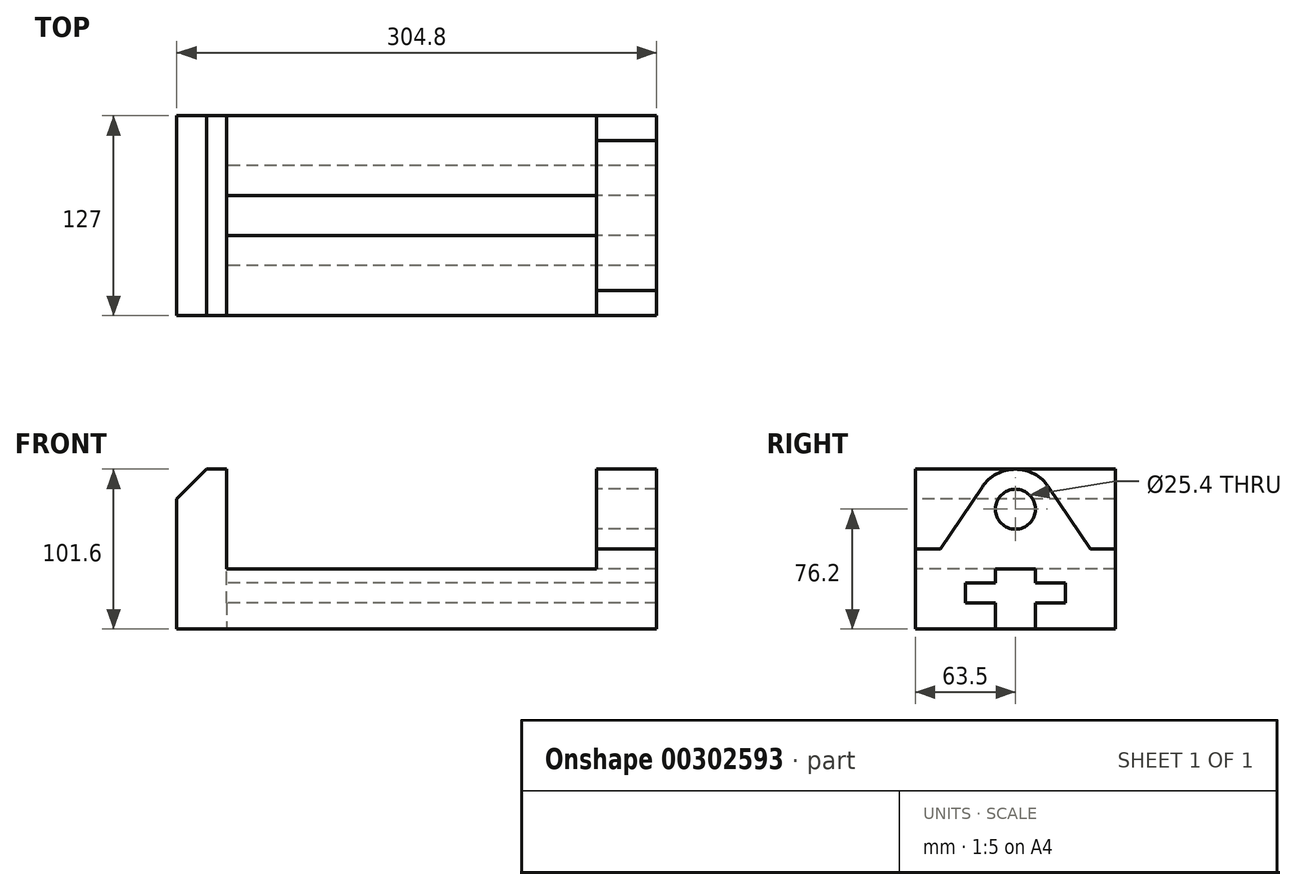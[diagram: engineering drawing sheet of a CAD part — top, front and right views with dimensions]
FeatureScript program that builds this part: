
annotation { "Feature Type Name" : "Feature", "Feature Type Description" : "" }
export const myFeature = defineFeature(function(context is Context, id is Id, definition is map)
    precondition{}
    {
        {
            var Q0;
            Q0=qCreatedBy(makeId("Right.planeOp"),FACE);
            var sketch = newSketch(context, id + "F0", { "sketchPlane" : qUnion([Q0])});
            skLineSegment(sketch, "E0.bottom", {"start": v(0, 101.6) * mm, "end": v(127, 101.6) * mm});
            skLineSegment(sketch, "E0.top", {"start": v(0, 0) * mm, "end": v(127, 0) * mm});
            skLineSegment(sketch, "E0.left", {"start": v(0, 101.6) * mm, "end": v(0, 0) * mm});
            skLineSegment(sketch, "E0.right", {"start": v(127, 101.6) * mm, "end": v(127, 0) * mm});
            skLineSegment(sketch, "E1", {"start": v(127, 50.8) * mm, "end": v(111.13, 50.8) * mm});
            skLineSegment(sketch, "E2", {"start": v(0, 0) * mm, "end": v(0, 50.8) * mm});
            skLineSegment(sketch, "E3", {"start": v(0, 50.8) * mm, "end": v(15.88, 50.8) * mm});
            skLineSegment(sketch, "E4", {"start": v(15.88, 50.8) * mm, "end": v(42.4, 90.35) * mm});
            skLineSegment(sketch, "E5", {"start": v(111.13, 50.8) * mm, "end": v(84.6, 90.35) * mm});
            skArc(sketch, "E6", {"start": v(42.4, 90.35) * mm, "mid": v(63.5, 101.6) * mm, "end": v(84.6, 90.35) * mm});
            skCircle(sketch, "E7", {"center": v(63.5, 76.2) * mm, "radius": 12.7 * mm});
            skLineSegment(sketch, "E8", {"start": v(50.8, 0) * mm, "end": v(50.8, 16.51) * mm});
            skLineSegment(sketch, "E9", {"start": v(50.8, 16.51) * mm, "end": v(31.75, 16.51) * mm});
            skLineSegment(sketch, "E10", {"start": v(31.75, 16.51) * mm, "end": v(31.75, 29.21) * mm});
            skLineSegment(sketch, "E11", {"start": v(31.75, 29.21) * mm, "end": v(50.8, 29.21) * mm});
            skLineSegment(sketch, "E12", {"start": v(50.8, 29.21) * mm, "end": v(50.8, 38.1) * mm});
            skLineSegment(sketch, "E13", {"start": v(50.8, 38.1) * mm, "end": v(76.2, 38.1) * mm});
            skLineSegment(sketch, "E14", {"start": v(76.2, 38.1) * mm, "end": v(76.2, 29.21) * mm});
            skLineSegment(sketch, "E15", {"start": v(76.2, 29.21) * mm, "end": v(95.25, 29.21) * mm});
            skLineSegment(sketch, "E16", {"start": v(95.25, 29.21) * mm, "end": v(95.25, 16.51) * mm});
            skLineSegment(sketch, "E17", {"start": v(95.25, 16.51) * mm, "end": v(76.2, 16.51) * mm});
            skLineSegment(sketch, "E18", {"start": v(76.2, 16.51) * mm, "end": v(76.2, 0) * mm});
            skLineSegment(sketch, "E19", {"start": v(76.2, 0) * mm, "end": v(50.8, 0) * mm});
            skLineSegment(sketch, "E20", {"start": v(63.5, 76.2) * mm, "end": v(63.5, -44.68) * mm, "construction": true});
            skPoint(sketch, "E20.endSnap0", {"position": v(63.5, 0) * mm});
            skSolve(sketch);
        }
        {
            var Q0;
            {var subQ8=sQuery(id+"F0.wireOp",EDGE,"E1");Q0=makeQuery(id+"F0.imprint","IMPRINT",FACE,{"disambiguationData":[TD([[makeQuery(id+"F0.imprint","IMPRINT",EDGE,{"derivedFrom":subQ8}),1.0]])]});}
            extrude(context, id + "F1", {"entities" : qUnion([Q0]), "depth" : 38.1 * mm});
        }
        {
            var Q0;
            Q0=makeQuery(id+"F1.opExtrude","CAP_FACE",FACE,{"disambiguationData":[OSD([sQuery(id+"F0.wireOp",EDGE,"E0.right"),sQuery(id+"F0.wireOp",EDGE,"E0.top"),sQuery(id+"F0.wireOp",EDGE,"E1"),sQuery(id+"F0.wireOp",EDGE,"E2"),sQuery(id+"F0.wireOp",EDGE,"E3"),sQuery(id+"F0.wireOp",EDGE,"E4"),sQuery(id+"F0.wireOp",EDGE,"E5"),sQuery(id+"F0.wireOp",EDGE,"E6"),sQuery(id+"F0.wireOp",EDGE,"E7"),sQuery(id+"F0.wireOp",EDGE,"E8"),sQuery(id+"F0.wireOp",EDGE,"E9"),sQuery(id+"F0.wireOp",EDGE,"E10"),sQuery(id+"F0.wireOp",EDGE,"E11"),sQuery(id+"F0.wireOp",EDGE,"E12"),sQuery(id+"F0.wireOp",EDGE,"E13"),sQuery(id+"F0.wireOp",EDGE,"E14"),sQuery(id+"F0.wireOp",EDGE,"E15"),sQuery(id+"F0.wireOp",EDGE,"E16"),sQuery(id+"F0.wireOp",EDGE,"E17"),sQuery(id+"F0.wireOp",EDGE,"E18")])],"isStart":true});
            var sketch = newSketch(context, id + "F2", { "sketchPlane" : qUnion([Q0])});
            skLineSegment(sketch, "E21", {"start": v(-127, 0) * mm, "end": v(-127, 38.1) * mm});
            skLineSegment(sketch, "E22", {"start": v(-127, 38.1) * mm, "end": v(-76.2, 38.1) * mm});
            skLineSegment(sketch, "E23", {"start": v(-50.8, 38.1) * mm, "end": v(0, 38.1) * mm});
            skLineSegment(sketch, "E24", {"start": v(0, 38.1) * mm, "end": v(0, 0) * mm});
            skLineSegment(sketch, "E25", {"start": v(0, 0) * mm, "end": v(-50.8, 0) * mm});
            skLineSegment(sketch, "E26", {"start": v(-50.8, 0) * mm, "end": v(-50.8, 16.51) * mm});
            skLineSegment(sketch, "E27", {"start": v(-50.8, 16.51) * mm, "end": v(-31.75, 16.51) * mm});
            skLineSegment(sketch, "E28", {"start": v(-31.75, 16.51) * mm, "end": v(-31.75, 29.21) * mm});
            skLineSegment(sketch, "E29", {"start": v(-31.75, 29.21) * mm, "end": v(-50.8, 29.21) * mm});
            skLineSegment(sketch, "E30", {"start": v(-50.8, 29.21) * mm, "end": v(-50.8, 38.1) * mm});
            skLineSegment(sketch, "E31", {"start": v(-76.2, 38.1) * mm, "end": v(-76.2, 29.21) * mm});
            skLineSegment(sketch, "E32", {"start": v(-76.2, 29.2) * mm, "end": v(-95.25, 29.21) * mm});
            skLineSegment(sketch, "E33", {"start": v(-95.25, 29.21) * mm, "end": v(-95.25, 16.51) * mm});
            skLineSegment(sketch, "E34", {"start": v(-95.25, 16.51) * mm, "end": v(-76.2, 16.51) * mm});
            skLineSegment(sketch, "E35", {"start": v(-76.2, 16.51) * mm, "end": v(-76.2, 0) * mm});
            skLineSegment(sketch, "E36", {"start": v(-76.2, 0) * mm, "end": v(-127, 0) * mm});
            skSolve(sketch);
        }
        {
            var Q0;
            Q0=makeQuery(id+"F2.imprint","IMPRINT",FACE,{"disambiguationData":[TD([[makeQuery(id+"F2.imprint","IMPRINT",EDGE,{"derivedFrom":sQuery(id+"F2.wireOp",EDGE,"E21")}),1.0]])]});
            extrude(context, id + "F3", {"entities" : qUnion([Q0]), "operationType" : NewBodyOperationType.ADD, "depth" : 234.95 * mm});
        }
        {
            var Q0;
            Q0=makeQuery(id+"F2.imprint","IMPRINT",FACE,{"disambiguationData":[TD([[makeQuery(id+"F2.imprint","IMPRINT",EDGE,{"derivedFrom":sQuery(id+"F2.wireOp",EDGE,"E23")}),-1.0]])]});
            extrude(context, id + "F4", {"entities" : qUnion([Q0]), "operationType" : NewBodyOperationType.ADD, "depth" : 234.95 * mm});
        }
        {
            var Q0;
            Q0=qCreatedBy(makeId("Right.planeOp"),FACE);
            cPlane(context, id + "F5", {"entities" : qUnion([Q0]), "cplaneType" : CPlaneType.OFFSET, "offset" : 234.95 * mm, "oppositeDirection" : true, "width" : 152.4 * mm, "height" : 152.4 * mm});
        }
        {
            var Q0;
            Q0=qCreatedBy(id+"F5.planeOp",FACE);
            var sketch = newSketch(context, id + "F6", { "sketchPlane" : qUnion([Q0])});
            skLineSegment(sketch, "E37.0.0", {"start": v(76.2, 38.1) * mm, "end": v(127, 38.1) * mm});
            skLineSegment(sketch, "E37.0.1", {"start": v(127, 38.1) * mm, "end": v(127, 0) * mm});
            skLineSegment(sketch, "E37.0.2", {"start": v(127, 0) * mm, "end": v(76.2, 0) * mm});
            skLineSegment(sketch, "E37.0.3", {"start": v(76.2, 0) * mm, "end": v(76.2, 16.51) * mm});
            skLineSegment(sketch, "E37.0.4", {"start": v(76.2, 16.51) * mm, "end": v(95.25, 16.51) * mm});
            skLineSegment(sketch, "E37.0.5", {"start": v(95.25, 16.51) * mm, "end": v(95.25, 29.21) * mm});
            skLineSegment(sketch, "E37.0.6", {"start": v(95.25, 29.21) * mm, "end": v(76.2, 29.21) * mm});
            skLineSegment(sketch, "E37.0.7", {"start": v(76.2, 29.21) * mm, "end": v(76.2, 38.1) * mm});
            skLineSegment(sketch, "E38.0.0", {"start": v(0, 38.1) * mm, "end": v(50.8, 38.1) * mm});
            skLineSegment(sketch, "E38.0.1", {"start": v(50.8, 38.1) * mm, "end": v(50.8, 29.21) * mm});
            skLineSegment(sketch, "E38.0.2", {"start": v(50.8, 29.21) * mm, "end": v(31.75, 29.21) * mm});
            skLineSegment(sketch, "E38.0.3", {"start": v(31.75, 29.21) * mm, "end": v(31.75, 16.51) * mm});
            skLineSegment(sketch, "E38.0.4", {"start": v(31.75, 16.51) * mm, "end": v(50.8, 16.51) * mm});
            skLineSegment(sketch, "E38.0.5", {"start": v(50.8, 16.51) * mm, "end": v(50.8, 0) * mm});
            skLineSegment(sketch, "E38.0.6", {"start": v(50.8, 0) * mm, "end": v(0, 0) * mm});
            skLineSegment(sketch, "E38.0.7", {"start": v(0, 0) * mm, "end": v(0, 38.1) * mm});
            skLineSegment(sketch, "E39", {"start": v(0, 0) * mm, "end": v(127, 0) * mm});
            skLineSegment(sketch, "E40", {"start": v(127, 101.6) * mm, "end": v(0, 101.6) * mm});
            skPoint(sketch, "E40.startSnap0", {"position": v(127, 19.05) * mm});
            skLineSegment(sketch, "E41", {"start": v(0, 101.6) * mm, "end": v(0, 0) * mm});
            skLineSegment(sketch, "E42", {"start": v(127, 101.6) * mm, "end": v(127, 0) * mm});
            skSolve(sketch);
        }
        {
            var Q0;
            {var subQ1=sQuery(id+"F6.wireOp",EDGE,"E37.0.0");Q0=makeQuery(id+"F6.imprint","IMPRINT",FACE,{"disambiguationData":[TD([[makeQuery(id+"F6.imprint","IMPRINT",EDGE,{"derivedFrom":subQ1}),1.0]])]});}
            var Q1;
            {var subQ0=sQuery(id+"F6.wireOp",EDGE,"E38.0.0");Q1=makeQuery(id+"F6.imprint","IMPRINT",FACE,{"disambiguationData":[TD([[makeQuery(id+"F6.imprint","IMPRINT",EDGE,{"derivedFrom":subQ0}),-1.0]])]});}
            var Q2;
            {var subQ4=sQuery(id+"F6.wireOp",EDGE,"E37.0.0");Q2=makeQuery(id+"F6.imprint","IMPRINT",FACE,{"disambiguationData":[TD([[makeQuery(id+"F6.imprint","IMPRINT",EDGE,{"derivedFrom":subQ4}),-1.0]])]});}
            extrude(context, id + "F7", {"entities" : qUnion([Q0, Q1, Q2]), "operationType" : NewBodyOperationType.ADD, "oppositeDirection" : true, "depth" : 31.75 * mm});
        }
        {
            var Q0;
            Q0=makeQuery(id+"F7.boolean.opBoolean","MERGE",FACE,{"derivedFrom":[makeQuery(id+"F4.boolean.opBoolean","MERGE",FACE,{"derivedFrom":[makeQuery(id+"F1.opExtrude","SWEPT_FACE",FACE,{"disambiguationData":[OSD([sQuery(id+"F0.wireOp",EDGE,"E2")])]}),makeQuery(id+"F4.opExtrude","SWEPT_FACE",FACE,{"disambiguationData":[OSD([sQuery(id+"F2.wireOp",EDGE,"E24")])]})]}),makeQuery(id+"F7.opExtrude","SWEPT_FACE",FACE,{"disambiguationData":[OSD([sQuery(id+"F6.wireOp",EDGE,"E41")])]})]});
            var sketch = newSketch(context, id + "F8", { "sketchPlane" : qUnion([Q0])});
            skLineSegment(sketch, "E43", {"start": v(-266.7, 82.55) * mm, "end": v(-247.65, 82.55) * mm});
            skPoint(sketch, "E43.endSnap0", {"position": v(-247.65, 101.6) * mm});
            skLineSegment(sketch, "E44", {"start": v(-247.65, 82.55) * mm, "end": v(-247.65, 101.6) * mm});
            skLineSegment(sketch, "E45", {"start": v(-266.7, 82.55) * mm, "end": v(-247.65, 101.6) * mm});
            skLineSegment(sketch, "E46", {"start": v(-247.65, 101.6) * mm, "end": v(-266.7, 101.6) * mm});
            skLineSegment(sketch, "E47", {"start": v(-266.7, 101.6) * mm, "end": v(-266.7, 82.55) * mm});
            skSolve(sketch);
        }
        {
            var Q0;
            Q0=makeQuery(id+"F8.imprint","IMPRINT",FACE,{"disambiguationData":[TD([[makeQuery(id+"F8.imprint","IMPRINT",EDGE,{"derivedFrom":sQuery(id+"F8.wireOp",EDGE,"E45")}),1.0]])]});
            extrude(context, id + "F9", {"entities" : qUnion([Q0]), "operationType" : NewBodyOperationType.REMOVE, "endBound" : BoundingType.THROUGH_ALL, "oppositeDirection" : true, "depth" : 25.4 * mm});
        }
    });
